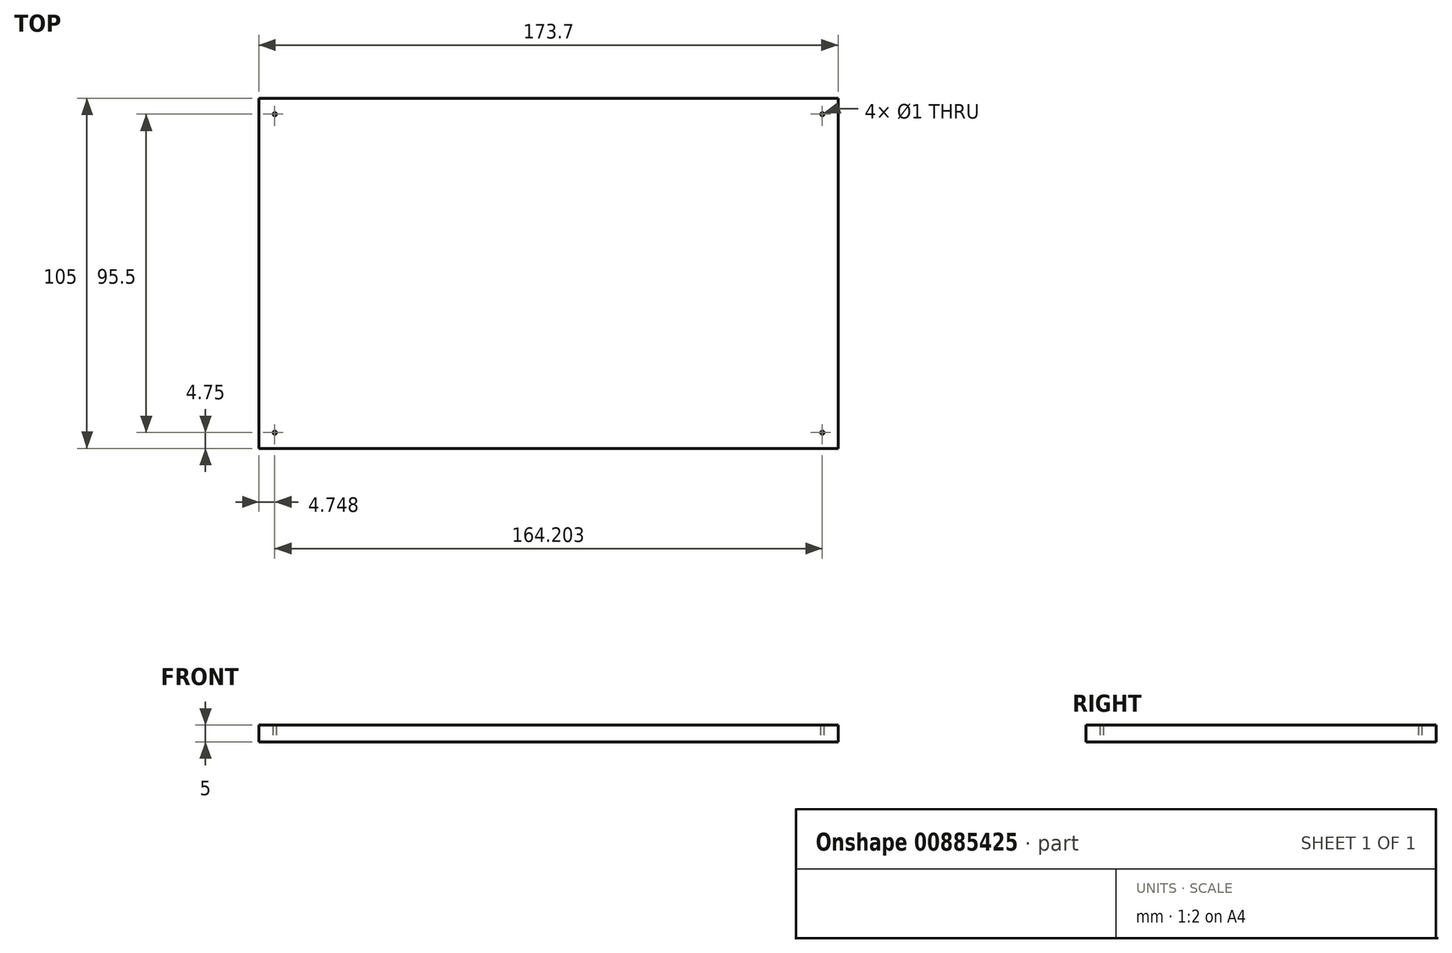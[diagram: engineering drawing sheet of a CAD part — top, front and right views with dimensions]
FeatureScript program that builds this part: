
annotation { "Feature Type Name" : "Feature", "Feature Type Description" : "" }
export const myFeature = defineFeature(function(context is Context, id is Id, definition is map)
    precondition{}
    {
        {
            var Q0;
            Q0=qCreatedBy(makeId("Top.planeOp"),FACE);
            var sketch = newSketch(context, id + "F0", { "sketchPlane" : qUnion([Q0])});
            skLineSegment(sketch, "E0.bottom", {"start": v(-77.35, 43) * mm, "end": v(77.35, 43) * mm});
            skLineSegment(sketch, "E0.top", {"start": v(-77.35, -43) * mm, "end": v(77.35, -43) * mm});
            skLineSegment(sketch, "E0.left", {"start": v(-77.35, 43) * mm, "end": v(-77.35, -43) * mm});
            skLineSegment(sketch, "E0.right", {"start": v(77.35, 43) * mm, "end": v(77.35, -43) * mm});
            skPoint(sketch, "E0.middle", {"position": v(0, 0) * mm});
            skSolve(sketch);
        }
        {
            var Q0;
            Q0=qCreatedBy(makeId("Top.planeOp"),FACE);
            var sketch = newSketch(context, id + "F1", { "sketchPlane" : qUnion([Q0])});
            skLineSegment(sketch, "E1.bottom", {"start": v(-82.1, 47.75) * mm, "end": v(82.1, 47.75) * mm, "construction": true});
            skLineSegment(sketch, "E1.top", {"start": v(-82.1, -47.75) * mm, "end": v(82.1, -47.75) * mm, "construction": true});
            skLineSegment(sketch, "E1.left", {"start": v(-82.1, 47.75) * mm, "end": v(-82.1, -47.75) * mm, "construction": true});
            skLineSegment(sketch, "E1.right", {"start": v(82.1, 47.75) * mm, "end": v(82.1, -47.75) * mm, "construction": true});
            skPoint(sketch, "E1.middle", {"position": v(0, 0) * mm});
            skCircle(sketch, "E2", {"center": v(-82.1, 47.75) * mm, "radius": 4.75 * mm, "construction": true});
            skCircle(sketch, "E3", {"center": v(82.1, 47.75) * mm, "radius": 4.75 * mm, "construction": true});
            skCircle(sketch, "E4", {"center": v(82.1, -47.75) * mm, "radius": 4.75 * mm, "construction": true});
            skCircle(sketch, "E5", {"center": v(-82.1, -47.75) * mm, "radius": 4.75 * mm, "construction": true});
            skLineSegment(sketch, "E6.bottom", {"start": v(-86.85, 52.5) * mm, "end": v(86.85, 52.5) * mm});
            skLineSegment(sketch, "E6.top", {"start": v(-86.85, -52.5) * mm, "end": v(86.85, -52.5) * mm});
            skLineSegment(sketch, "E6.left", {"start": v(-86.85, 52.5) * mm, "end": v(-86.85, -52.5) * mm});
            skLineSegment(sketch, "E6.right", {"start": v(86.85, 52.5) * mm, "end": v(86.85, -52.5) * mm});
            skCircle(sketch, "E7", {"center": v(-82.1, 47.75) * mm, "radius": 0.5 * mm});
            skCircle(sketch, "E8", {"center": v(82.1, 47.75) * mm, "radius": 0.5 * mm});
            skCircle(sketch, "E9.MirrorC", {"center": v(82.1, -47.75) * mm, "radius": 0.5 * mm});
            skCircle(sketch, "E10.MirrorC", {"center": v(-82.1, -47.75) * mm, "radius": 0.5 * mm});
            skSolve(sketch);
        }
        {
            var Q0;
            Q0=makeQuery(id+"F1.imprint","IMPRINT",FACE,{"disambiguationData":[TD([[makeQuery(id+"F1.imprint","IMPRINT",EDGE,{"derivedFrom":sQuery(id+"F1.wireOp",EDGE,"E6.bottom")}),-1.0]])]});
            extrude(context, id + "F2", {"entities" : qUnion([Q0]), "depth" : 5 * mm, "offsetDistance" : 25 * mm});
        }
    });
